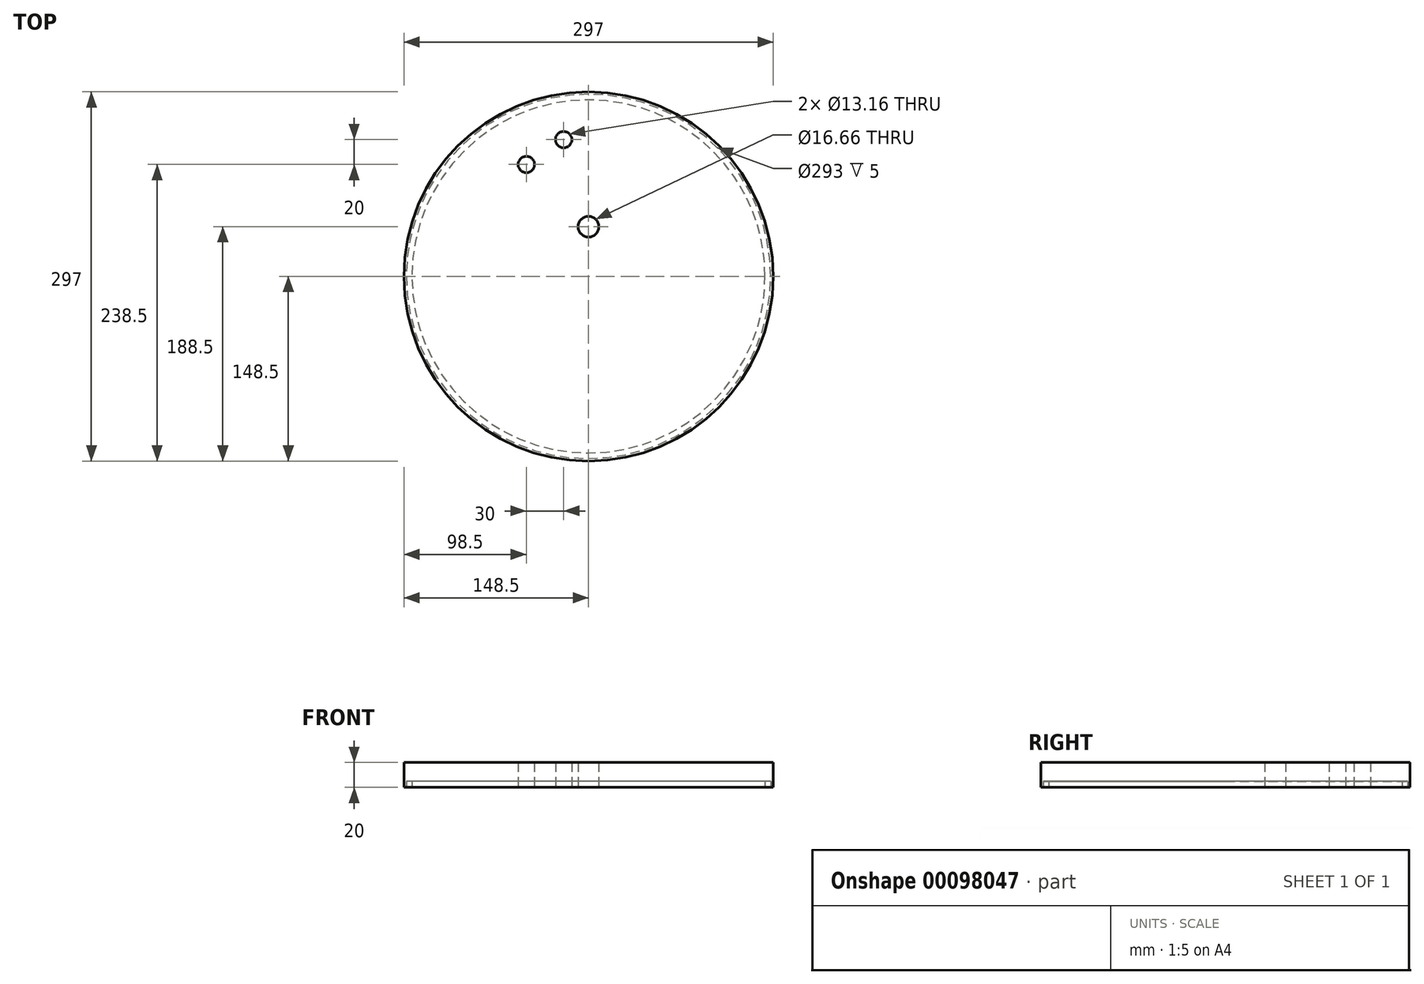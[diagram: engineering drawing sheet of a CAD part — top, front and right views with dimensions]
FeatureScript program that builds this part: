
annotation { "Feature Type Name" : "Feature", "Feature Type Description" : "" }
export const myFeature = defineFeature(function(context is Context, id is Id, definition is map)
    precondition{}
    {
        {
            var Q0;
            Q0=qCreatedBy(makeId("Top.planeOp"),FACE);
            var sketch = newSketch(context, id + "F0", { "sketchPlane" : qUnion([Q0])});
            skCircle(sketch, "E0", {"center": v(0, 0) * mm, "radius": 148.5 * mm});
            skCircle(sketch, "E1", {"center": v(-50, 90) * mm, "radius": 6.58 * mm});
            skCircle(sketch, "E2", {"center": v(-20, 110) * mm, "radius": 6.58 * mm});
            skCircle(sketch, "E3", {"center": v(0, 40) * mm, "radius": 8.33 * mm});
            skLineSegment(sketch, "E4", {"start": v(0, 40) * mm, "end": v(0, 0) * mm, "construction": true});
            skLineSegment(sketch, "E5", {"start": v(0, 40) * mm, "end": v(0, 84.9) * mm, "construction": true});
            skLineSegment(sketch, "E6", {"start": v(0, 40) * mm, "end": v(-40, 40) * mm, "construction": true});
            skLineSegment(sketch, "E7", {"start": v(-40, 40) * mm, "end": v(-40, 100) * mm, "construction": true});
            skLineSegment(sketch, "E8", {"start": v(-40, 100) * mm, "end": v(100, 100) * mm, "construction": true});
            skLineSegment(sketch, "E9", {"start": v(100, 100) * mm, "end": v(100, 40) * mm, "construction": true});
            skLineSegment(sketch, "E10", {"start": v(100, 40) * mm, "end": v(0, 40) * mm, "construction": true});
            skSolve(sketch);
        }
        {
            var Q0;
            Q0=makeQuery(id+"F0.imprint","IMPRINT",FACE,{"disambiguationData":[TD([[makeQuery(id+"F0.imprint","IMPRINT",EDGE,{"derivedFrom":sQuery(id+"F0.wireOp",EDGE,"E0")}),1.0]])]});
            var Q1;
            Q1=makeQuery(id+"F0.imprint","IMPRINT",FACE,{"disambiguationData":[TD([[makeQuery(id+"F0.imprint","IMPRINT",EDGE,{"derivedFrom":sQuery(id+"F0.wireOp",EDGE,"LIXrByum-44Gz-KbWN-PE50-DMeDG7NppI0J")}),1.0]])]});
            var Q2;
            Q2=makeQuery(id+"F0.imprint","IMPRINT",FACE,{"disambiguationData":[TD([[makeQuery(id+"F0.imprint","IMPRINT",EDGE,{"derivedFrom":sQuery(id+"F0.wireOp",EDGE,"oq2Y4278-V4UZ-WgQw-2GIa-DsGsglEtdsp5")}),1.0]])]});
            extrude(context, id + "F1", {"entities" : qUnion([Q0, Q1, Q2]), "depth" : 20 * mm});
        }
        {
            var Q0;
            Q0=makeQuery(id+"F0.imprint","IMPRINT",FACE,{"disambiguationData":[TD([[makeQuery(id+"F0.imprint","IMPRINT",EDGE,{"derivedFrom":sQuery(id+"F0.wireOp",EDGE,"E0")}),1.0]])]});
            var sketch = newSketch(context, id + "F2", { "sketchPlane" : qUnion([Q0])});
            skCircle(sketch, "E11", {"center": v(0, 0) * mm, "radius": 146.5 * mm});
            skCircle(sketch, "E12", {"center": v(0, 0) * mm, "radius": 142 * mm});
            skSolve(sketch);
        }
        {
            var Q0;
            Q0=qSketchRegion(id+"F2",true);
            extrude(context, id + "F3", {"entities" : qUnion([Q0]), "operationType" : NewBodyOperationType.REMOVE, "depth" : 5 * mm});
        }
    });
